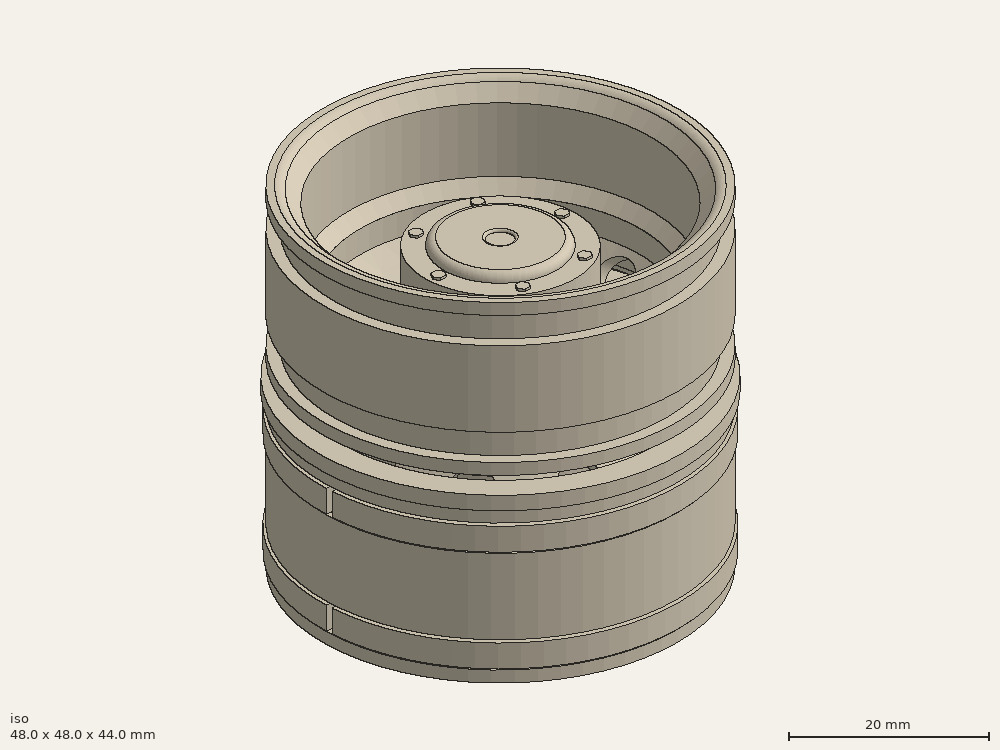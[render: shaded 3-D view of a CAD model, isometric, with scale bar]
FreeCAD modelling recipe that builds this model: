
FCSTD DOCUMENT  (FreeCAD 0.18.4R)
Label: wheel_rear_02
License: CC-BY 3.0
LicenseURL: http://creativecommons.org/licenses/by/3.0/
objects: Part::Cylinder×94, Part::MultiFuse×48, Part::Cut×33, Part::Mirroring×11, Part::Fillet×8, Part::Feature×7, Part::Extrusion×7, Part::Chamfer×5, Part::Cone×4
note: 217 computed .brp shape members not serialized (recipe doc carries the construction recipe); baked Part::Feature solids carry a one-line shape summary decoded from their .brp

FEATURE [Part::Cylinder] Cylinder
  Angle = 360
  AttacherType = Attacher::AttachEngine3D
  Height = 12
  Radius = 20
FEATURE [Part::Cylinder] Cylinder001
  Angle = 360
  AttacherType = Attacher::AttachEngine3D
  Height = 8
  Placement = pos=(12,0,16) rot=(0,1,0;1.01229rad)
  Radius = 2.5
FEATURE [Part::Cylinder] Cylinder002
  Angle = 360
  AttacherType = Attacher::AttachEngine3D
  Height = 8
  Placement = pos=(12,0,16) rot=(0,1,0;1.01229rad)
  Radius = 2.5
FEATURE [Part::Mirroring] Part__Mirroring  label="Cylinder107 (Mirror #1)004"
  Base = (0,0,0)
  Normal = (1,0,0)
  Source = -> Cylinder002
FEATURE [Part::MultiFuse] Fusion002
  Refine = true
  Shapes = -> [Cylinder001,Part__Mirroring]
FEATURE [Part::Cylinder] Cylinder003
  Angle = 360
  AttacherType = Attacher::AttachEngine3D
  Height = 8
  Placement = pos=(12,0,16) rot=(0,1,0;1.01229rad)
  Radius = 2.5
FEATURE [Part::Cylinder] Cylinder004
  Angle = 360
  AttacherType = Attacher::AttachEngine3D
  Height = 8
  Placement = pos=(12,0,16) rot=(0,1,0;1.01229rad)
  Radius = 2.5
FEATURE [Part::Mirroring] Part__Mirroring001  label="Cylinder107 (Mirror #1)005"
  Base = (0,0,0)
  Normal = (1,0,0)
  Source = -> Cylinder004
FEATURE [Part::MultiFuse] Fusion003
  Placement = pos=(0,0,0) rot=(0,0,1;0.628319rad)
  Refine = true
  Shapes = -> [Cylinder003,Part__Mirroring001]
FEATURE [Part::Cylinder] Cylinder005
  Angle = 360
  AttacherType = Attacher::AttachEngine3D
  Height = 8
  Placement = pos=(12,0,16) rot=(0,1,0;1.01229rad)
  Radius = 2.5
FEATURE [Part::Cylinder] Cylinder006
  Angle = 360
  AttacherType = Attacher::AttachEngine3D
  Height = 8
  Placement = pos=(12,0,16) rot=(0,1,0;1.01229rad)
  Radius = 2.5
FEATURE [Part::Mirroring] Part__Mirroring002  label="Cylinder107 (Mirror #1)006"
  Base = (0,0,0)
  Normal = (1,0,0)
  Source = -> Cylinder006
FEATURE [Part::MultiFuse] Fusion004
  Placement = pos=(0,0,0) rot=(0,0,1;1.25664rad)
  Refine = true
  Shapes = -> [Cylinder005,Part__Mirroring002]
FEATURE [Part::Cylinder] Cylinder007
  Angle = 360
  AttacherType = Attacher::AttachEngine3D
  Height = 8
  Placement = pos=(12,0,16) rot=(0,1,0;1.01229rad)
  Radius = 2.5
FEATURE [Part::Cylinder] Cylinder008
  Angle = 360
  AttacherType = Attacher::AttachEngine3D
  Height = 8
  Placement = pos=(12,0,16) rot=(0,1,0;1.01229rad)
  Radius = 2.5
FEATURE [Part::Mirroring] Part__Mirroring003  label="Cylinder107 (Mirror #1)007"
  Base = (0,0,0)
  Normal = (1,0,0)
  Source = -> Cylinder008
FEATURE [Part::MultiFuse] Fusion005
  Placement = pos=(0,0,0) rot=(0,0,1;1.88496rad)
  Refine = true
  Shapes = -> [Cylinder007,Part__Mirroring003]
FEATURE [Part::Cylinder] Cylinder009
  Angle = 360
  AttacherType = Attacher::AttachEngine3D
  Height = 8
  Placement = pos=(12,0,16) rot=(0,1,0;1.01229rad)
  Radius = 2.5
FEATURE [Part::Cylinder] Cylinder010
  Angle = 360
  AttacherType = Attacher::AttachEngine3D
  Height = 8
  Placement = pos=(12,0,16) rot=(0,1,0;1.01229rad)
  Radius = 2.5
FEATURE [Part::Mirroring] Part__Mirroring004  label="Cylinder107 (Mirror #1)008"
  Base = (0,0,0)
  Normal = (1,0,0)
  Source = -> Cylinder010
FEATURE [Part::MultiFuse] Fusion006
  Placement = pos=(0,0,0) rot=(0,0,1;2.51327rad)
  Refine = true
  Shapes = -> [Cylinder009,Part__Mirroring004]
FEATURE [Part::MultiFuse] Fusion001
  Placement = pos=(0,0,-1) rot=(0,0,1;0rad)
  Refine = true
  Shapes = -> [Fusion002,Fusion003,Fusion004,Fusion005,Fusion006]
FEATURE [Part::Cylinder] Cylinder011
  Angle = 360
  AttacherType = Attacher::AttachEngine3D
  Height = 10
  Placement = pos=(12.5,0,13) rot=(0,0,1;0rad)
  Radius = 1.1
FEATURE [Part::Cylinder] Cylinder012
  Angle = 360
  AttacherType = Attacher::AttachEngine3D
  Height = 10
  Placement = pos=(-12.5,0,13) rot=(0,0,1;0rad)
  Radius = 1.1
FEATURE [Part::MultiFuse] Fusion008
  Placement = pos=(0,0,0) rot=(0,0,1;0.314159rad)
  Refine = true
  Shapes = -> [Cylinder011,Cylinder012]
FEATURE [Part::Cylinder] Cylinder013
  Angle = 360
  AttacherType = Attacher::AttachEngine3D
  Height = 10
  Placement = pos=(12.5,0,13) rot=(0,0,1;0rad)
  Radius = 1.1
FEATURE [Part::Cylinder] Cylinder014
  Angle = 360
  AttacherType = Attacher::AttachEngine3D
  Height = 10
  Placement = pos=(-12.5,0,13) rot=(0,0,1;0rad)
  Radius = 1.1
FEATURE [Part::MultiFuse] Fusion009
  Placement = pos=(0,0,0) rot=(0,0,1;0.942478rad)
  Refine = true
  Shapes = -> [Cylinder013,Cylinder014]
FEATURE [Part::Cylinder] Cylinder015
  Angle = 360
  AttacherType = Attacher::AttachEngine3D
  Height = 10
  Placement = pos=(12.5,0,13) rot=(0,0,1;0rad)
  Radius = 1.1
FEATURE [Part::Cylinder] Cylinder016
  Angle = 360
  AttacherType = Attacher::AttachEngine3D
  Height = 10
  Placement = pos=(-12.5,0,13) rot=(0,0,1;0rad)
  Radius = 1.1
FEATURE [Part::MultiFuse] Fusion010
  Placement = pos=(0,0,0) rot=(0,0,1;2.82743rad)
  Refine = true
  Shapes = -> [Cylinder015,Cylinder016]
FEATURE [Part::Cylinder] Cylinder017
  Angle = 360
  AttacherType = Attacher::AttachEngine3D
  Height = 10
  Placement = pos=(12.5,0,13) rot=(0,0,1;0rad)
  Radius = 1.1
FEATURE [Part::Cylinder] Cylinder018
  Angle = 360
  AttacherType = Attacher::AttachEngine3D
  Height = 10
  Placement = pos=(-12.5,0,13) rot=(0,0,1;0rad)
  Radius = 1.1
FEATURE [Part::MultiFuse] Fusion011
  Placement = pos=(0,0,0) rot=(0,0,1;2.19911rad)
  Refine = true
  Shapes = -> [Cylinder017,Cylinder018]
FEATURE [Part::Cylinder] Cylinder019
  Angle = 360
  AttacherType = Attacher::AttachEngine3D
  Height = 10
  Placement = pos=(12.5,0,13) rot=(0,0,1;0rad)
  Radius = 1.1
FEATURE [Part::Cylinder] Cylinder020
  Angle = 360
  AttacherType = Attacher::AttachEngine3D
  Height = 10
  Placement = pos=(-12.5,0,13) rot=(0,0,1;0rad)
  Radius = 1.1
FEATURE [Part::MultiFuse] Fusion012
  Placement = pos=(0,0,0) rot=(0,0,1;1.5708rad)
  Refine = true
  Shapes = -> [Cylinder019,Cylinder020]
FEATURE [Part::MultiFuse] Fusion007
  Refine = true
  Shapes = -> [Fusion008,Fusion009,Fusion010,Fusion011,Fusion012]
FEATURE [Part::Cylinder] Cylinder021
  Angle = 360
  AttacherType = Attacher::AttachEngine3D
  Height = 10
  Placement = pos=(0,0,0.5) rot=(0,0,1;0rad)
  Radius = 23.5
FEATURE [Part::Cylinder] Cylinder022
  Angle = 360
  AttacherType = Attacher::AttachEngine3D
  Height = 17
  Radius = 22
FEATURE [Part::Cut] Cut005
  Base = -> Cylinder021
  Placement = pos=(0,0,4.5) rot=(0,0,1;0rad)
  Refine = true
  Tool = -> Cylinder022
FEATURE [Part::Cylinder] Cylinder023
  Angle = 360
  AttacherType = Attacher::AttachEngine3D
  Height = 20
  Radius = 23.5
FEATURE [Part::Cylinder] Cylinder024
  Angle = 360
  AttacherType = Attacher::AttachEngine3D
  Height = 17
  Radius = 23.5
FEATURE [Part::Cylinder] Cylinder025
  Angle = 360
  AttacherType = Attacher::AttachEngine3D
  Height = 17
  Radius = 22.1
FEATURE [Part::Cut] Cut007
  Base = -> Cylinder024
  Placement = pos=(0,0,1.5) rot=(0,0,1;0rad)
  Refine = true
  Tool = -> Cylinder025
FEATURE [Part::Cut] Cut006
  Base = -> Cylinder023
  Refine = true
  Tool = -> Cut007
FEATURE [Part::MultiFuse] Fusion013
  Refine = true
  Shapes = -> [Cut005,Cut006]
FEATURE [Part::Cylinder] Cylinder026
  Angle = 360
  AttacherType = Attacher::AttachEngine3D
  Height = 20
  Radius = 18.5
FEATURE [Part::Cut] Cut004
  Base = -> Fusion013
  Refine = true
  Tool = -> Cylinder026
FEATURE [Part::Cylinder] Cylinder027
  Angle = 360
  AttacherType = Attacher::AttachEngine3D
  Height = 10
  Placement = pos=(0,0,15) rot=(0,0,1;0rad)
  Radius = 20.5
FEATURE [Part::Cut] Cut003
  Base = -> Cut004
  Refine = true
  Tool = -> Cylinder027
FEATURE [Part::Fillet] Fillet002
  Base = -> Cut003
  Edges = 1 edges r=1: [Edge20]
FEATURE [Part::Cone] Cone
  Angle = 360
  AttacherType = Attacher::AttachEngine3D
  Height = 7
  Placement = pos=(0,0,15) rot=(0,0,1;0rad)
  Radius1 = 21
  Radius2 = 15
FEATURE [Part::Cylinder] Cylinder028
  Angle = 360
  AttacherType = Attacher::AttachEngine3D
  Height = 26
  Radius = 10
FEATURE [Part::Cut] Cut009
  Base = -> Cone
  Refine = true
  Tool = -> Cylinder028
FEATURE [Part::Cone] Cone001
  Angle = 360
  AttacherType = Attacher::AttachEngine3D
  Height = 10
  Placement = pos=(0,0,9) rot=(0,0,1;0rad)
  Radius1 = 24
  Radius2 = 15
FEATURE [Part::Cut] Cut008
  Base = -> Cut009
  Refine = true
  Tool = -> Cone001
FEATURE [Part::MultiFuse] Fusion
  Refine = true
  Shapes = -> [Fillet002,Cut008]
FEATURE [Part::Cut] Cut002
  Base = -> Fusion
  Refine = true
  Tool = -> Cylinder
FEATURE [Part::Chamfer] Chamfer001
  Base = -> Cut002
  Edges = 1 edges r=1.49: [Edge39]
FEATURE [Part::Chamfer] Chamfer
  Base = -> Chamfer001
  Edges = 1 edges r=2: [Edge10]
FEATURE [Part::Cut] Cut001
  Base = -> Chamfer
  Refine = true
  Tool = -> Fusion001
FEATURE [Part::Cut] Cut
  Base = -> Cut001
  Refine = true
  Tool = -> Fusion007
FEATURE [Part::Fillet] Fillet001
  Base = -> Cut
  Edges = 1 edges r=1.5: [Edge121]
FEATURE [Part::Fillet] Fillet  label="rim_internal_"
  Base = -> Fillet001
  Edges = 1 edges r=1.5: [Edge161]
FEATURE [Part::Cylinder] Cylinder029
  Angle = 360
  AttacherType = Attacher::AttachEngine3D
  Height = 3
  Placement = pos=(0,0,12) rot=(0,0,1;0.139626rad)
  Radius = 18.4
FEATURE [Part::Cylinder] Cylinder030
  Angle = 360
  AttacherType = Attacher::AttachEngine3D
  Height = 3
  Placement = pos=(0,0,12) rot=(0,0,1;1.39626rad)
  Radius = 18.4
FEATURE [Part::Cylinder] Cylinder031
  Angle = 360
  AttacherType = Attacher::AttachEngine3D
  Height = 3
  Placement = pos=(0,0,12) rot=(0,0,1;2.6529rad)
  Radius = 18.4
FEATURE [Part::Cylinder] Cylinder032
  Angle = 360
  AttacherType = Attacher::AttachEngine3D
  Height = 3
  Placement = pos=(0,0,12) rot=(0,0,1;3.90954rad)
  Radius = 18.4
FEATURE [Part::Cylinder] Cylinder033
  Angle = 360
  AttacherType = Attacher::AttachEngine3D
  Height = 3
  Placement = pos=(0,0,12) rot=(0,0,-1;1.11701rad)
  Radius = 18.4
FEATURE [Part::MultiFuse] Fusion015
  Refine = true
  Shapes = -> [Cylinder029,Cylinder030,Cylinder031,Cylinder032,Cylinder033]
FEATURE [Part::Cylinder] Cylinder034
  Angle = 360
  AttacherType = Attacher::AttachEngine3D
  Height = 4
  Placement = pos=(0,0,15) rot=(0,0,1;0rad)
  Radius = 15
FEATURE [Part::Cylinder] Cylinder035
  Angle = 360
  AttacherType = Attacher::AttachEngine3D
  Height = 10
  Placement = pos=(0,0,19) rot=(0,0,1;0rad)
  Radius = 10
FEATURE [Part::Cylinder] Cylinder036
  Angle = 360
  AttacherType = Attacher::AttachEngine3D
  Height = 5
  Placement = pos=(0,0,24) rot=(0,0,1;0rad)
  Radius = 8
FEATURE [Part::Cut] Cut013
  Base = -> Cylinder035
  Refine = true
  Tool = -> Cylinder036
FEATURE [Part::MultiFuse] Fusion017
  Refine = true
  Shapes = -> [Cylinder034,Cut013]
FEATURE [Part::Cylinder] Cylinder037
  Angle = 360
  AttacherType = Attacher::AttachEngine3D
  Height = 10
  Placement = pos=(0,0,21) rot=(0,0,1;0rad)
  Radius = 2
FEATURE [Part::Cut] Cut012
  Base = -> Fusion017
  Refine = true
  Tool = -> Cylinder037
FEATURE [Part::Cylinder] Cylinder038
  Angle = 360
  AttacherType = Attacher::AttachEngine3D
  Height = 3
  Placement = pos=(0,0,12) rot=(0,0,1;0rad)
  Radius = 15
FEATURE [Part::MultiFuse] Fusion016
  Refine = true
  Shapes = -> [Cut012,Cylinder038]
FEATURE [Part::MultiFuse] Fusion014
  Refine = true
  Shapes = -> [Fusion015,Fusion016]
FEATURE [Part::Feature] Face
  shape: bbox 17.79 x 17.28 x 2e-07 mm, 1 faces, 0 solids (baked)
FEATURE [Part::Extrusion] Extrude
  Base = -> Face
  Dir = (0,0,6)
  DirMode = 0
  FaceMakerClass = Part::FaceMakerExtrusion
  LengthFwd = 0
  LengthRev = 0
  Placement = pos=(0,0,15) rot=(0,0,1;0rad)
  Solid = false
  Symmetric = false
FEATURE [Part::Cylinder] Cylinder039
  Angle = 360
  AttacherType = Attacher::AttachEngine3D
  Height = 3
  Placement = pos=(0,0,12) rot=(0,0,1;0rad)
  Radius = 11
FEATURE [Part::MultiFuse] Fusion018
  Refine = true
  Shapes = -> [Extrude,Cylinder039]
FEATURE [Part::Cut] Cut011
  Base = -> Fusion014
  Refine = true
  Tool = -> Fusion018
FEATURE [Part::Cylinder] Cylinder040
  Angle = 360
  AttacherType = Attacher::AttachEngine3D
  Height = 10
  Placement = pos=(12.5,0,13) rot=(0,0,1;0rad)
  Radius = 0.8
FEATURE [Part::Cylinder] Cylinder041
  Angle = 360
  AttacherType = Attacher::AttachEngine3D
  Height = 10
  Placement = pos=(-12.5,0,13) rot=(0,0,1;0rad)
  Radius = 0.8
FEATURE [Part::MultiFuse] Fusion020
  Placement = pos=(0,0,0) rot=(0,0,1;0.314159rad)
  Refine = true
  Shapes = -> [Cylinder040,Cylinder041]
FEATURE [Part::Cylinder] Cylinder042
  Angle = 360
  AttacherType = Attacher::AttachEngine3D
  Height = 10
  Placement = pos=(12.5,0,13) rot=(0,0,1;0rad)
  Radius = 0.8
FEATURE [Part::Cylinder] Cylinder043
  Angle = 360
  AttacherType = Attacher::AttachEngine3D
  Height = 10
  Placement = pos=(-12.5,0,13) rot=(0,0,1;0rad)
  Radius = 0.8
FEATURE [Part::MultiFuse] Fusion021
  Placement = pos=(0,0,0) rot=(0,0,1;0.942478rad)
  Refine = true
  Shapes = -> [Cylinder042,Cylinder043]
FEATURE [Part::Cylinder] Cylinder044
  Angle = 360
  AttacherType = Attacher::AttachEngine3D
  Height = 10
  Placement = pos=(12.5,0,13) rot=(0,0,1;0rad)
  Radius = 0.8
FEATURE [Part::Cylinder] Cylinder045
  Angle = 360
  AttacherType = Attacher::AttachEngine3D
  Height = 10
  Placement = pos=(-12.5,0,13) rot=(0,0,1;0rad)
  Radius = 0.8
FEATURE [Part::MultiFuse] Fusion022
  Placement = pos=(0,0,0) rot=(0,0,1;2.82743rad)
  Refine = true
  Shapes = -> [Cylinder044,Cylinder045]
FEATURE [Part::Cylinder] Cylinder046
  Angle = 360
  AttacherType = Attacher::AttachEngine3D
  Height = 10
  Placement = pos=(12.5,0,13) rot=(0,0,1;0rad)
  Radius = 0.8
FEATURE [Part::Cylinder] Cylinder047
  Angle = 360
  AttacherType = Attacher::AttachEngine3D
  Height = 10
  Placement = pos=(-12.5,0,13) rot=(0,0,1;0rad)
  Radius = 0.8
FEATURE [Part::MultiFuse] Fusion023
  Placement = pos=(0,0,0) rot=(0,0,1;2.19911rad)
  Refine = true
  Shapes = -> [Cylinder046,Cylinder047]
FEATURE [Part::Cylinder] Cylinder048
  Angle = 360
  AttacherType = Attacher::AttachEngine3D
  Height = 10
  Placement = pos=(12.5,0,13) rot=(0,0,1;0rad)
  Radius = 0.8
FEATURE [Part::Cylinder] Cylinder049
  Angle = 360
  AttacherType = Attacher::AttachEngine3D
  Height = 10
  Placement = pos=(-12.5,0,13) rot=(0,0,1;0rad)
  Radius = 0.8
FEATURE [Part::MultiFuse] Fusion024
  Placement = pos=(0,0,0) rot=(0,0,1;1.5708rad)
  Refine = true
  Shapes = -> [Cylinder048,Cylinder049]
FEATURE [Part::MultiFuse] Fusion019
  Placement = pos=(0,0,-2) rot=(0,0,1;0rad)
  Refine = true
  Shapes = -> [Fusion020,Fusion021,Fusion022,Fusion023,Fusion024]
FEATURE [Part::Cylinder] Cylinder050
  Angle = 360
  AttacherType = Attacher::AttachEngine3D
  Height = 8
  Placement = pos=(0,0,29) rot=(0,0,1;0rad)
  Radius = 10
FEATURE [Part::Cylinder] Cylinder051
  Angle = 360
  AttacherType = Attacher::AttachEngine3D
  Height = 5
  Placement = pos=(0,0,25) rot=(0,0,1;0rad)
  Radius = 8
FEATURE [Part::MultiFuse] Fusion026
  Refine = true
  Shapes = -> [Cylinder050,Cylinder051]
FEATURE [Part::Cylinder] Cylinder052
  Angle = 360
  AttacherType = Attacher::AttachEngine3D
  Height = 6
  Placement = pos=(0,0,25) rot=(0,0,1;0rad)
  Radius = 6
FEATURE [Part::Cut] Cut014
  Base = -> Fusion026
  Refine = true
  Tool = -> Cylinder052
FEATURE [Part::Cylinder] Cylinder053
  Angle = 360
  AttacherType = Attacher::AttachEngine3D
  Height = 2
  Placement = pos=(0,0,-6) rot=(0,0,1;0rad)
  Radius = 7.5
FEATURE [Part::Fillet] Fillet004
  Base = -> Cylinder053
  Edges = 1 edges r=1: [Edge1]
  Placement = pos=(0,0,-6) rot=(0,0,1;0rad)
FEATURE [Part::Cylinder] Cylinder054
  Angle = 360
  AttacherType = Attacher::AttachEngine3D
  Height = 0.3
  Placement = pos=(0,0,-10.3) rot=(0,0,1;0rad)
  Radius = 1.5
FEATURE [Part::Cut] Cut015
  Base = -> Fillet004
  Refine = true
  Tool = -> Cylinder054
FEATURE [Part::Fillet] Fillet003
  Base = -> Cut015
  Edges = 1 edges r=0.29: [Edge6]
  Placement = pos=(0,0,48) rot=(0,0,1;0rad)
FEATURE [Part::Feature] Face001
  shape: bbox 1.791 x 1.578 x 2e-07 mm, 1 faces, 0 solids (baked)
FEATURE [Part::Extrusion] Extrude001
  Base = -> Face001
  Dir = (0,0,0.3)
  DirMode = 0
  FaceMakerClass = Part::FaceMakerExtrusion
  LengthFwd = 0
  LengthRev = 0
  Placement = pos=(-0.75,0,47.5) rot=(0,0,1;3.14159rad)
  Solid = false
  Symmetric = false
FEATURE [Part::Feature] Face002
  shape: bbox 1.791 x 1.578 x 2e-07 mm, 1 faces, 0 solids (baked)
FEATURE [Part::Extrusion] Extrude002
  Base = -> Face002
  Dir = (0,0,0.3)
  DirMode = 0
  FaceMakerClass = Part::FaceMakerExtrusion
  LengthFwd = 0
  LengthRev = 0
  Placement = pos=(0.75,0,47.5) rot=(0,0,1;0rad)
  Solid = false
  Symmetric = false
FEATURE [Part::MultiFuse] Fusion027
  Placement = pos=(0,0,0) rot=(0,0,1;4.18879rad)
  Refine = true
  Shapes = -> [Extrude001,Extrude002]
FEATURE [Part::Feature] Face003
  shape: bbox 1.791 x 1.578 x 2e-07 mm, 1 faces, 0 solids (baked)
FEATURE [Part::Extrusion] Extrude003
  Base = -> Face003
  Dir = (0,0,0.3)
  DirMode = 0
  FaceMakerClass = Part::FaceMakerExtrusion
  LengthFwd = 0
  LengthRev = 0
  Placement = pos=(-0.75,0,47.5) rot=(0,0,1;3.14159rad)
  Solid = false
  Symmetric = false
FEATURE [Part::Feature] Face004
  shape: bbox 1.791 x 1.578 x 2e-07 mm, 1 faces, 0 solids (baked)
FEATURE [Part::Extrusion] Extrude004
  Base = -> Face004
  Dir = (0,0,0.3)
  DirMode = 0
  FaceMakerClass = Part::FaceMakerExtrusion
  LengthFwd = 0
  LengthRev = 0
  Placement = pos=(0.75,0,47.5) rot=(0,0,1;0rad)
  Solid = false
  Symmetric = false
FEATURE [Part::MultiFuse] Fusion028
  Placement = pos=(0,0,0) rot=(0,0,1;2.0944rad)
  Refine = true
  Shapes = -> [Extrude003,Extrude004]
FEATURE [Part::Feature] Face005
  shape: bbox 1.791 x 1.578 x 2e-07 mm, 1 faces, 0 solids (baked)
FEATURE [Part::Extrusion] Extrude005
  Base = -> Face005
  Dir = (0,0,0.3)
  DirMode = 0
  FaceMakerClass = Part::FaceMakerExtrusion
  LengthFwd = 0
  LengthRev = 0
  Placement = pos=(-0.75,0,47.5) rot=(0,0,1;3.14159rad)
  Solid = false
  Symmetric = false
FEATURE [Part::Feature] Face006
  shape: bbox 1.791 x 1.578 x 2e-07 mm, 1 faces, 0 solids (baked)
FEATURE [Part::Extrusion] Extrude006
  Base = -> Face006
  Dir = (0,0,0.3)
  DirMode = 0
  FaceMakerClass = Part::FaceMakerExtrusion
  LengthFwd = 0
  LengthRev = 0
  Placement = pos=(0.75,0,47.5) rot=(0,0,1;0rad)
  Solid = false
  Symmetric = false
FEATURE [Part::MultiFuse] Fusion029
  Refine = true
  Shapes = -> [Extrude005,Extrude006]
FEATURE [Part::MultiFuse] Fusion025  label="hub-cap-rear-00"
  Refine = true
  Shapes = -> [Cut014,Fillet003,Fusion027,Fusion028,Fusion029]
FEATURE [Part::Cylinder] Cylinder055
  Angle = 360
  AttacherType = Attacher::AttachEngine3D
  Height = 10
  Placement = pos=(0,0,0.5) rot=(0,0,1;0rad)
  Radius = 23.5
FEATURE [Part::Cylinder] Cylinder056
  Angle = 360
  AttacherType = Attacher::AttachEngine3D
  Height = 17
  Radius = 22
FEATURE [Part::Cut] Cut021
  Base = -> Cylinder055
  Placement = pos=(0,0,4.5) rot=(0,0,1;0rad)
  Refine = true
  Tool = -> Cylinder056
FEATURE [Part::Cylinder] Cylinder057
  Angle = 360
  AttacherType = Attacher::AttachEngine3D
  Height = 20
  Radius = 23.5
FEATURE [Part::Cylinder] Cylinder058
  Angle = 360
  AttacherType = Attacher::AttachEngine3D
  Height = 17
  Radius = 23.5
FEATURE [Part::Cylinder] Cylinder059
  Angle = 360
  AttacherType = Attacher::AttachEngine3D
  Height = 17
  Radius = 22.1
FEATURE [Part::Cut] Cut023
  Base = -> Cylinder058
  Placement = pos=(0,0,1.5) rot=(0,0,1;0rad)
  Refine = true
  Tool = -> Cylinder059
FEATURE [Part::Cut] Cut022
  Base = -> Cylinder057
  Refine = true
  Tool = -> Cut023
FEATURE [Part::MultiFuse] Fusion031
  Refine = true
  Shapes = -> [Cut021,Cut022]
FEATURE [Part::Cylinder] Cylinder060
  Angle = 360
  AttacherType = Attacher::AttachEngine3D
  Height = 20
  Radius = 18.5
FEATURE [Part::Cut] Cut020
  Base = -> Fusion031
  Refine = true
  Tool = -> Cylinder060
FEATURE [Part::Cylinder] Cylinder061
  Angle = 360
  AttacherType = Attacher::AttachEngine3D
  Height = 10
  Placement = pos=(0,0,15) rot=(0,0,1;0rad)
  Radius = 20.5
FEATURE [Part::Cut] Cut019
  Base = -> Cut020
  Refine = true
  Tool = -> Cylinder061
FEATURE [Part::Fillet] Fillet007
  Base = -> Cut019
  Edges = 1 edges r=1: [Edge20]
FEATURE [Part::Cone] Cone002
  Angle = 360
  AttacherType = Attacher::AttachEngine3D
  Height = 7
  Placement = pos=(0,0,15) rot=(0,0,1;0rad)
  Radius1 = 21
  Radius2 = 15
FEATURE [Part::Cylinder] Cylinder062
  Angle = 360
  AttacherType = Attacher::AttachEngine3D
  Height = 26
  Radius = 10
FEATURE [Part::Cut] Cut025
  Base = -> Cone002
  Refine = true
  Tool = -> Cylinder062
FEATURE [Part::Cone] Cone003
  Angle = 360
  AttacherType = Attacher::AttachEngine3D
  Height = 10
  Placement = pos=(0,0,9) rot=(0,0,1;0rad)
  Radius1 = 24
  Radius2 = 15
FEATURE [Part::Cut] Cut024
  Base = -> Cut025
  Refine = true
  Tool = -> Cone003
FEATURE [Part::MultiFuse] Fusion030
  Refine = true
  Shapes = -> [Fillet007,Cut024]
FEATURE [Part::Cylinder] Cylinder063
  Angle = 360
  AttacherType = Attacher::AttachEngine3D
  Height = 12
  Radius = 20
FEATURE [Part::Cut] Cut018
  Base = -> Fusion030
  Refine = true
  Tool = -> Cylinder063
FEATURE [Part::Chamfer] Chamfer003
  Base = -> Cut018
  Edges = 1 edges r=1.49: [Edge39]
FEATURE [Part::Chamfer] Chamfer002
  Base = -> Chamfer003
  Edges = 1 edges r=2: [Edge10]
FEATURE [Part::Cylinder] Cylinder064
  Angle = 360
  AttacherType = Attacher::AttachEngine3D
  Height = 8
  Placement = pos=(12,0,16) rot=(0,1,0;1.01229rad)
  Radius = 2.5
FEATURE [Part::Cylinder] Cylinder065
  Angle = 360
  AttacherType = Attacher::AttachEngine3D
  Height = 8
  Placement = pos=(12,0,16) rot=(0,1,0;1.01229rad)
  Radius = 2.5
FEATURE [Part::Mirroring] Part__Mirroring005  label="Cylinder107 (Mirror #1)009"
  Base = (0,0,0)
  Normal = (1,0,0)
  Source = -> Cylinder065
FEATURE [Part::MultiFuse] Fusion033
  Refine = true
  Shapes = -> [Cylinder064,Part__Mirroring005]
FEATURE [Part::Cylinder] Cylinder066
  Angle = 360
  AttacherType = Attacher::AttachEngine3D
  Height = 8
  Placement = pos=(12,0,16) rot=(0,1,0;1.01229rad)
  Radius = 2.5
FEATURE [Part::Cylinder] Cylinder067
  Angle = 360
  AttacherType = Attacher::AttachEngine3D
  Height = 8
  Placement = pos=(12,0,16) rot=(0,1,0;1.01229rad)
  Radius = 2.5
FEATURE [Part::Mirroring] Part__Mirroring006  label="Cylinder107 (Mirror #1)010"
  Base = (0,0,0)
  Normal = (1,0,0)
  Source = -> Cylinder067
FEATURE [Part::MultiFuse] Fusion034
  Placement = pos=(0,0,0) rot=(0,0,1;0.628319rad)
  Refine = true
  Shapes = -> [Cylinder066,Part__Mirroring006]
FEATURE [Part::Cylinder] Cylinder068
  Angle = 360
  AttacherType = Attacher::AttachEngine3D
  Height = 8
  Placement = pos=(12,0,16) rot=(0,1,0;1.01229rad)
  Radius = 2.5
FEATURE [Part::Cylinder] Cylinder069
  Angle = 360
  AttacherType = Attacher::AttachEngine3D
  Height = 8
  Placement = pos=(12,0,16) rot=(0,1,0;1.01229rad)
  Radius = 2.5
FEATURE [Part::Mirroring] Part__Mirroring007  label="Cylinder107 (Mirror #1)011"
  Base = (0,0,0)
  Normal = (1,0,0)
  Source = -> Cylinder069
FEATURE [Part::MultiFuse] Fusion035
  Placement = pos=(0,0,0) rot=(0,0,1;1.25664rad)
  Refine = true
  Shapes = -> [Cylinder068,Part__Mirroring007]
FEATURE [Part::Cylinder] Cylinder070
  Angle = 360
  AttacherType = Attacher::AttachEngine3D
  Height = 8
  Placement = pos=(12,0,16) rot=(0,1,0;1.01229rad)
  Radius = 2.5
FEATURE [Part::Cylinder] Cylinder071
  Angle = 360
  AttacherType = Attacher::AttachEngine3D
  Height = 8
  Placement = pos=(12,0,16) rot=(0,1,0;1.01229rad)
  Radius = 2.5
FEATURE [Part::Mirroring] Part__Mirroring008  label="Cylinder107 (Mirror #1)012"
  Base = (0,0,0)
  Normal = (1,0,0)
  Source = -> Cylinder071
FEATURE [Part::MultiFuse] Fusion036
  Placement = pos=(0,0,0) rot=(0,0,1;1.88496rad)
  Refine = true
  Shapes = -> [Cylinder070,Part__Mirroring008]
FEATURE [Part::Cylinder] Cylinder072
  Angle = 360
  AttacherType = Attacher::AttachEngine3D
  Height = 8
  Placement = pos=(12,0,16) rot=(0,1,0;1.01229rad)
  Radius = 2.5
FEATURE [Part::Cylinder] Cylinder073
  Angle = 360
  AttacherType = Attacher::AttachEngine3D
  Height = 8
  Placement = pos=(12,0,16) rot=(0,1,0;1.01229rad)
  Radius = 2.5
FEATURE [Part::Mirroring] Part__Mirroring009  label="Cylinder107 (Mirror #1)013"
  Base = (0,0,0)
  Normal = (1,0,0)
  Source = -> Cylinder073
FEATURE [Part::MultiFuse] Fusion037
  Placement = pos=(0,0,0) rot=(0,0,1;2.51327rad)
  Refine = true
  Shapes = -> [Cylinder072,Part__Mirroring009]
FEATURE [Part::MultiFuse] Fusion032
  Placement = pos=(0,0,-1) rot=(0,0,1;0rad)
  Refine = true
  Shapes = -> [Fusion033,Fusion034,Fusion035,Fusion036,Fusion037]
FEATURE [Part::Cut] Cut017
  Base = -> Chamfer002
  Refine = true
  Tool = -> Fusion032
FEATURE [Part::Cylinder] Cylinder074
  Angle = 360
  AttacherType = Attacher::AttachEngine3D
  Height = 10
  Placement = pos=(12.5,0,13) rot=(0,0,1;0rad)
  Radius = 1.1
FEATURE [Part::Cylinder] Cylinder075
  Angle = 360
  AttacherType = Attacher::AttachEngine3D
  Height = 10
  Placement = pos=(-12.5,0,13) rot=(0,0,1;0rad)
  Radius = 1.1
FEATURE [Part::MultiFuse] Fusion039
  Placement = pos=(0,0,0) rot=(0,0,1;0.314159rad)
  Refine = true
  Shapes = -> [Cylinder074,Cylinder075]
FEATURE [Part::Cylinder] Cylinder076
  Angle = 360
  AttacherType = Attacher::AttachEngine3D
  Height = 10
  Placement = pos=(12.5,0,13) rot=(0,0,1;0rad)
  Radius = 1.1
FEATURE [Part::Cylinder] Cylinder077
  Angle = 360
  AttacherType = Attacher::AttachEngine3D
  Height = 10
  Placement = pos=(-12.5,0,13) rot=(0,0,1;0rad)
  Radius = 1.1
FEATURE [Part::MultiFuse] Fusion040
  Placement = pos=(0,0,0) rot=(0,0,1;0.942478rad)
  Refine = true
  Shapes = -> [Cylinder076,Cylinder077]
FEATURE [Part::Cylinder] Cylinder078
  Angle = 360
  AttacherType = Attacher::AttachEngine3D
  Height = 10
  Placement = pos=(12.5,0,13) rot=(0,0,1;0rad)
  Radius = 1.1
FEATURE [Part::Cylinder] Cylinder079
  Angle = 360
  AttacherType = Attacher::AttachEngine3D
  Height = 10
  Placement = pos=(-12.5,0,13) rot=(0,0,1;0rad)
  Radius = 1.1
FEATURE [Part::MultiFuse] Fusion041
  Placement = pos=(0,0,0) rot=(0,0,1;2.82743rad)
  Refine = true
  Shapes = -> [Cylinder078,Cylinder079]
FEATURE [Part::Cylinder] Cylinder080
  Angle = 360
  AttacherType = Attacher::AttachEngine3D
  Height = 10
  Placement = pos=(12.5,0,13) rot=(0,0,1;0rad)
  Radius = 1.1
FEATURE [Part::Cylinder] Cylinder081
  Angle = 360
  AttacherType = Attacher::AttachEngine3D
  Height = 10
  Placement = pos=(-12.5,0,13) rot=(0,0,1;0rad)
  Radius = 1.1
FEATURE [Part::MultiFuse] Fusion042
  Placement = pos=(0,0,0) rot=(0,0,1;2.19911rad)
  Refine = true
  Shapes = -> [Cylinder080,Cylinder081]
FEATURE [Part::Cylinder] Cylinder082
  Angle = 360
  AttacherType = Attacher::AttachEngine3D
  Height = 10
  Placement = pos=(12.5,0,13) rot=(0,0,1;0rad)
  Radius = 1.1
FEATURE [Part::Cylinder] Cylinder083
  Angle = 360
  AttacherType = Attacher::AttachEngine3D
  Height = 10
  Placement = pos=(-12.5,0,13) rot=(0,0,1;0rad)
  Radius = 1.1
FEATURE [Part::MultiFuse] Fusion043
  Placement = pos=(0,0,0) rot=(0,0,1;1.5708rad)
  Refine = true
  Shapes = -> [Cylinder082,Cylinder083]
FEATURE [Part::MultiFuse] Fusion038
  Refine = true
  Shapes = -> [Fusion039,Fusion040,Fusion041,Fusion042,Fusion043]
FEATURE [Part::Cut] Cut016
  Base = -> Cut017
  Refine = true
  Tool = -> Fusion038
FEATURE [Part::Fillet] Fillet006
  Base = -> Cut016
  Edges = 1 edges r=1.5: [Edge121]
FEATURE [Part::Fillet] Fillet005  label="rim_internal001"
  Base = -> Fillet006
  Edges = 1 edges r=1.5: [Edge161]
FEATURE [Part::Mirroring] Part__Mirroring010  label="rim_external_"
  Base = (0,0,0)
  Normal = (0,0,1)
  Placement = pos=(0,0,44) rot=(0,0,1;0rad)
  Source = -> Fillet005
FEATURE [Part::Cylinder] Cylinder084
  Angle = 178
  AttacherType = Attacher::AttachEngine3D
  Height = 3
  Placement = pos=(0,0,1.8) rot=(0,0,1;0rad)
  Radius = 23.8
FEATURE [Part::Cylinder] Cylinder085
  Angle = 360
  AttacherType = Attacher::AttachEngine3D
  Height = 17
  Radius = 22.45
FEATURE [Part::Cut] Cut026
  Base = -> Cylinder084
  Refine = true
  Tool = -> Cylinder085
FEATURE [Part::Cylinder] Cylinder086
  Angle = 178
  AttacherType = Attacher::AttachEngine3D
  Height = 3
  Placement = pos=(0,0,1.8) rot=(0,0,1;0rad)
  Radius = 23.8
FEATURE [Part::Cylinder] Cylinder087
  Angle = 360
  AttacherType = Attacher::AttachEngine3D
  Height = 17
  Radius = 22.45
FEATURE [Part::Cut] Cut027
  Base = -> Cylinder086
  Placement = pos=(0,0,0) rot=(0,0,1;3.14159rad)
  Refine = true
  Tool = -> Cylinder087
FEATURE [Part::MultiFuse] Fusion045
  Placement = pos=(0,0,13.5) rot=(0,0,1;0rad)
  Refine = true
  Shapes = -> [Cut026,Cut027]
FEATURE [Part::Cut] Cut028
  Base = -> Cylinder086
  Placement = pos=(0,0,0) rot=(0,0,1;3.14159rad)
  Refine = true
  Tool = -> Cylinder087
FEATURE [Part::Cut] Cut029
  Base = -> Cylinder084
  Refine = true
  Tool = -> Cylinder085
FEATURE [Part::MultiFuse] Fusion046
  Refine = true
  Shapes = -> [Cut029,Cut028]
FEATURE [Part::MultiFuse] Fusion044  label="rim-support-all"
  Refine = true
  Shapes = -> [Fusion045,Fusion046]
FEATURE [Part::Cylinder] Cylinder088
  Angle = 360
  AttacherType = Attacher::AttachEngine3D
  Height = 1.8
  Placement = pos=(0,0,20) rot=(0,0,1;0rad)
  Radius = 24
FEATURE [Part::Cylinder] Cylinder089
  Angle = 360
  AttacherType = Attacher::AttachEngine3D
  Height = 2
  Placement = pos=(0,0,20) rot=(0,0,1;0rad)
  Radius = 21
FEATURE [Part::Cut] Cut030  label="rim-support"
  Base = -> Cylinder088
  Placement = pos=(0,0,0.2) rot=(0,0,1;0rad)
  Refine = true
  Tool = -> Cylinder089
FEATURE [Part::Cylinder] Cylinder090
  Angle = 360
  AttacherType = Attacher::AttachEngine3D
  Height = 26
  Radius = 10.1
FEATURE [Part::Cylinder] Cylinder091
  Angle = 360
  AttacherType = Attacher::AttachEngine3D
  Height = 26
  Radius = 10.1
FEATURE [Part::Cut] Cut031  label="rim_internal"
  Base = -> Fillet
  Refine = true
  Tool = -> Cylinder090
FEATURE [Part::Cut] Cut032  label="rim_external"
  Base = -> Part__Mirroring010
  Refine = true
  Tool = -> Cylinder091
FEATURE [Part::Cut] Cut033  label="hub-rear"
  Base = -> Cut011
  Refine = true
  Tool = -> Fusion019
FEATURE [Part::Cylinder] Cylinder092
  Angle = 360
  AttacherType = Attacher::AttachEngine3D
  Height = 2.8
  Placement = pos=(0,0,12) rot=(0,0,1;0rad)
  Radius = 10
FEATURE [Part::Cylinder] Cylinder093
  Angle = 360
  AttacherType = Attacher::AttachEngine3D
  Height = 8.8
  Placement = pos=(0,0,12) rot=(0,0,1;0rad)
  Radius = 5
FEATURE [Part::MultiFuse] Fusion047
  Refine = true
  Shapes = -> [Cylinder092,Cylinder093]
FEATURE [Part::Chamfer] Chamfer004  label="hub-rear-support"
  Base = -> Fusion047
  Edges = 1 edges r=0.75: [Edge3]
